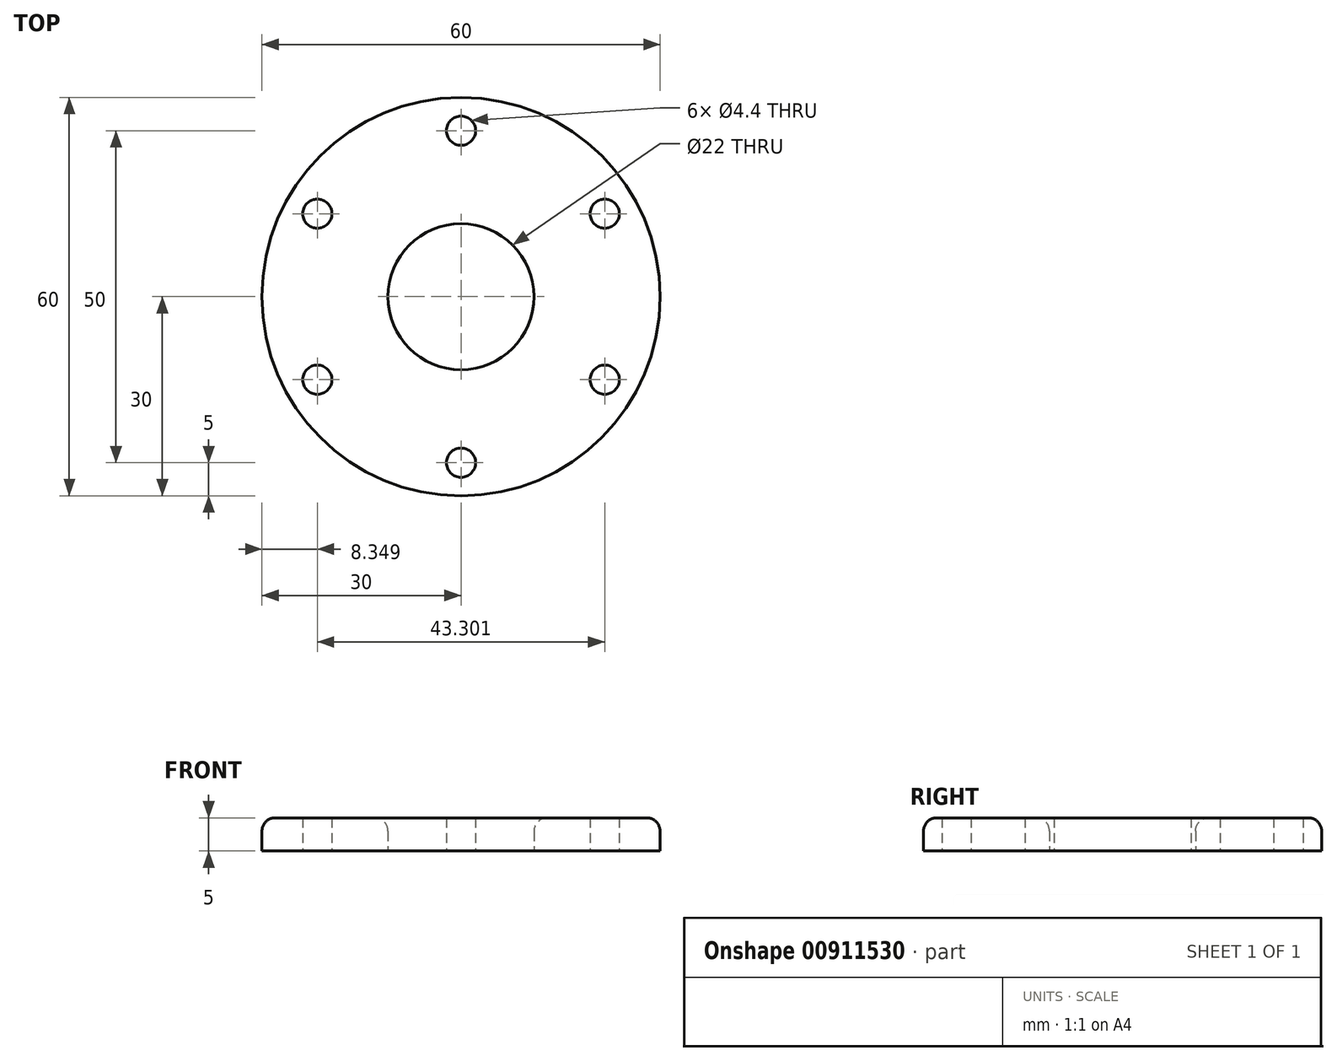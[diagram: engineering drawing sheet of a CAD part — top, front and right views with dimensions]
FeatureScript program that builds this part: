
annotation { "Feature Type Name" : "Feature", "Feature Type Description" : "" }
export const myFeature = defineFeature(function(context is Context, id is Id, definition is map)
    precondition{}
    {
        {
            var Q0;
            Q0=qCreatedBy(makeId("Top.planeOp"),FACE);
            var sketch = newSketch(context, id + "F0", { "sketchPlane" : qUnion([Q0])});
            skCircle(sketch, "E0", {"center": v(0, 0) * mm, "radius": 30 * mm});
            skCircle(sketch, "E1", {"center": v(0, 0) * mm, "radius": 11 * mm});
            skPoint(sketch, "E2", {"position": v(0, 25) * mm});
            skCircle(sketch, "E3", {"center": v(0, 25) * mm, "radius": 2.2 * mm});
            skCircle(sketch, "E4.1.0", {"center": v(-21.65, 12.5) * mm, "radius": 2.2 * mm});
            skCircle(sketch, "E4.2.0", {"center": v(-21.65, -12.5) * mm, "radius": 2.2 * mm});
            skCircle(sketch, "E4.3.0", {"center": v(0, -25) * mm, "radius": 2.2 * mm});
            skCircle(sketch, "E4.4.0", {"center": v(21.65, -12.5) * mm, "radius": 2.2 * mm});
            skCircle(sketch, "E4.5.0", {"center": v(21.65, 12.5) * mm, "radius": 2.2 * mm});
            skSolve(sketch);
        }
        {
            var Q0;
            Q0=makeQuery(id+"F0.imprint","IMPRINT",FACE,{"disambiguationData":[TD([[makeQuery(id+"F0.imprint","IMPRINT",EDGE,{"derivedFrom":sQuery(id+"F0.wireOp",EDGE,"E0")}),1.0]])]});
            extrude(context, id + "F1", {"entities" : qUnion([Q0]), "depth" : 5 * mm, "offsetDistance" : 25 * mm});
        }
        {
            var Q0;
            Q0=makeQuery(id+"F1.opExtrude","CAP_EDGE",EDGE,{"disambiguationData":[OSD([sQuery(id+"F0.wireOp",EDGE,"E0")])],"isStart":false});
            fillet(context, id + "F2", {"entities" : qUnion([Q0]), "radius" : 2 * mm, "tangentPropagation" : true, "allowEdgeOverflow" : false});
        }
        {
            var Q0;
            Q0=makeQuery(id+"F1.opExtrude","CAP_EDGE",EDGE,{"disambiguationData":[OSD([sQuery(id+"F0.wireOp",EDGE,"E1")])],"isStart":false});
            fillet(context, id + "F3", {"entities" : qUnion([Q0]), "radius" : 2 * mm, "tangentPropagation" : true, "allowEdgeOverflow" : false});
        }
    });
